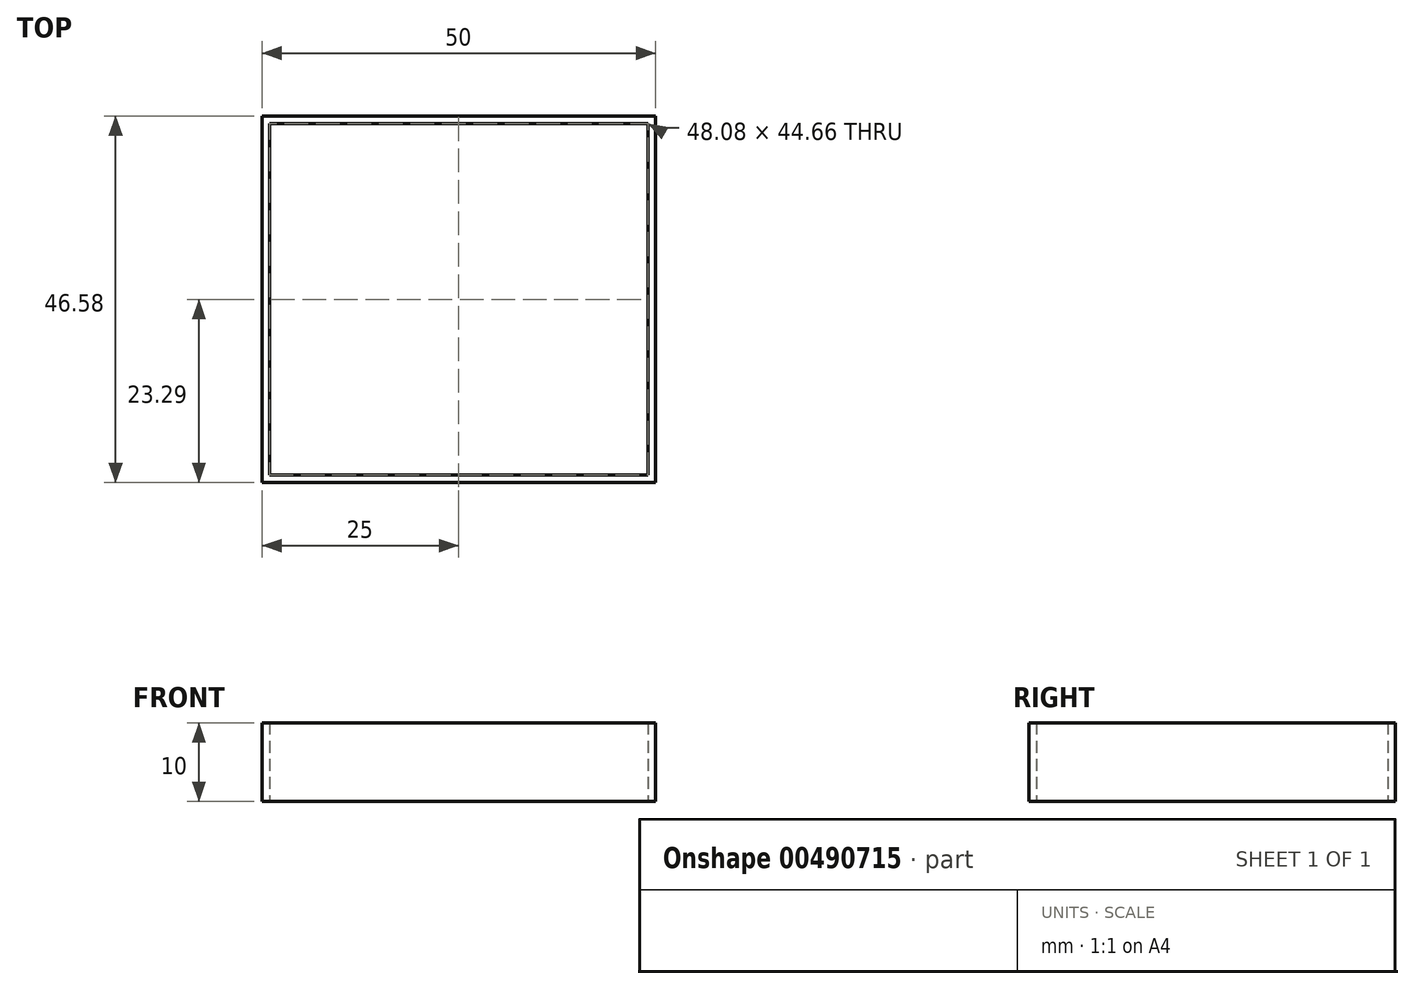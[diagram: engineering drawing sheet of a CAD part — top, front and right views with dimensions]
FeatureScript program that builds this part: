
annotation { "Feature Type Name" : "Feature", "Feature Type Description" : "" }
export const myFeature = defineFeature(function(context is Context, id is Id, definition is map)
    precondition{}
    {
        {
            var Q0;
            Q0=qCreatedBy(makeId("Top.planeOp"),FACE);
            var sketch = newSketch(context, id + "F0", { "sketchPlane" : qUnion([Q0])});
            skLineSegment(sketch, "E0.bottom", {"start": v(25, 23.3) * mm, "end": v(-25, 23.3) * mm});
            skLineSegment(sketch, "E0.top", {"start": v(25, -23.3) * mm, "end": v(-25, -23.3) * mm});
            skLineSegment(sketch, "E0.left", {"start": v(25, 23.3) * mm, "end": v(25, -23.3) * mm});
            skLineSegment(sketch, "E0.right", {"start": v(-25, 23.3) * mm, "end": v(-25, -23.3) * mm});
            skPoint(sketch, "E0.middle", {"position": v(0, 0) * mm});
            skLineSegment(sketch, "E1.bottom", {"start": v(24.04, 22.33) * mm, "end": v(-24.04, 22.33) * mm});
            skLineSegment(sketch, "E1.top", {"start": v(24.04, -22.33) * mm, "end": v(-24.04, -22.33) * mm});
            skLineSegment(sketch, "E1.left", {"start": v(24.04, 22.33) * mm, "end": v(24.04, -22.33) * mm});
            skLineSegment(sketch, "E1.right", {"start": v(-24.04, 22.33) * mm, "end": v(-24.04, -22.33) * mm});
            skSolve(sketch);
        }
        {
            var Q0;
            Q0=makeQuery(id+"F0.imprint","IMPRINT",FACE,{"disambiguationData":[TD([[makeQuery(id+"F0.imprint","IMPRINT",EDGE,{"derivedFrom":sQuery(id+"F0.wireOp",EDGE,"E0.bottom")}),1.0]])]});
            extrude(context, id + "F1", {"entities" : qUnion([Q0]), "depth" : 10 * mm});
        }
    });
